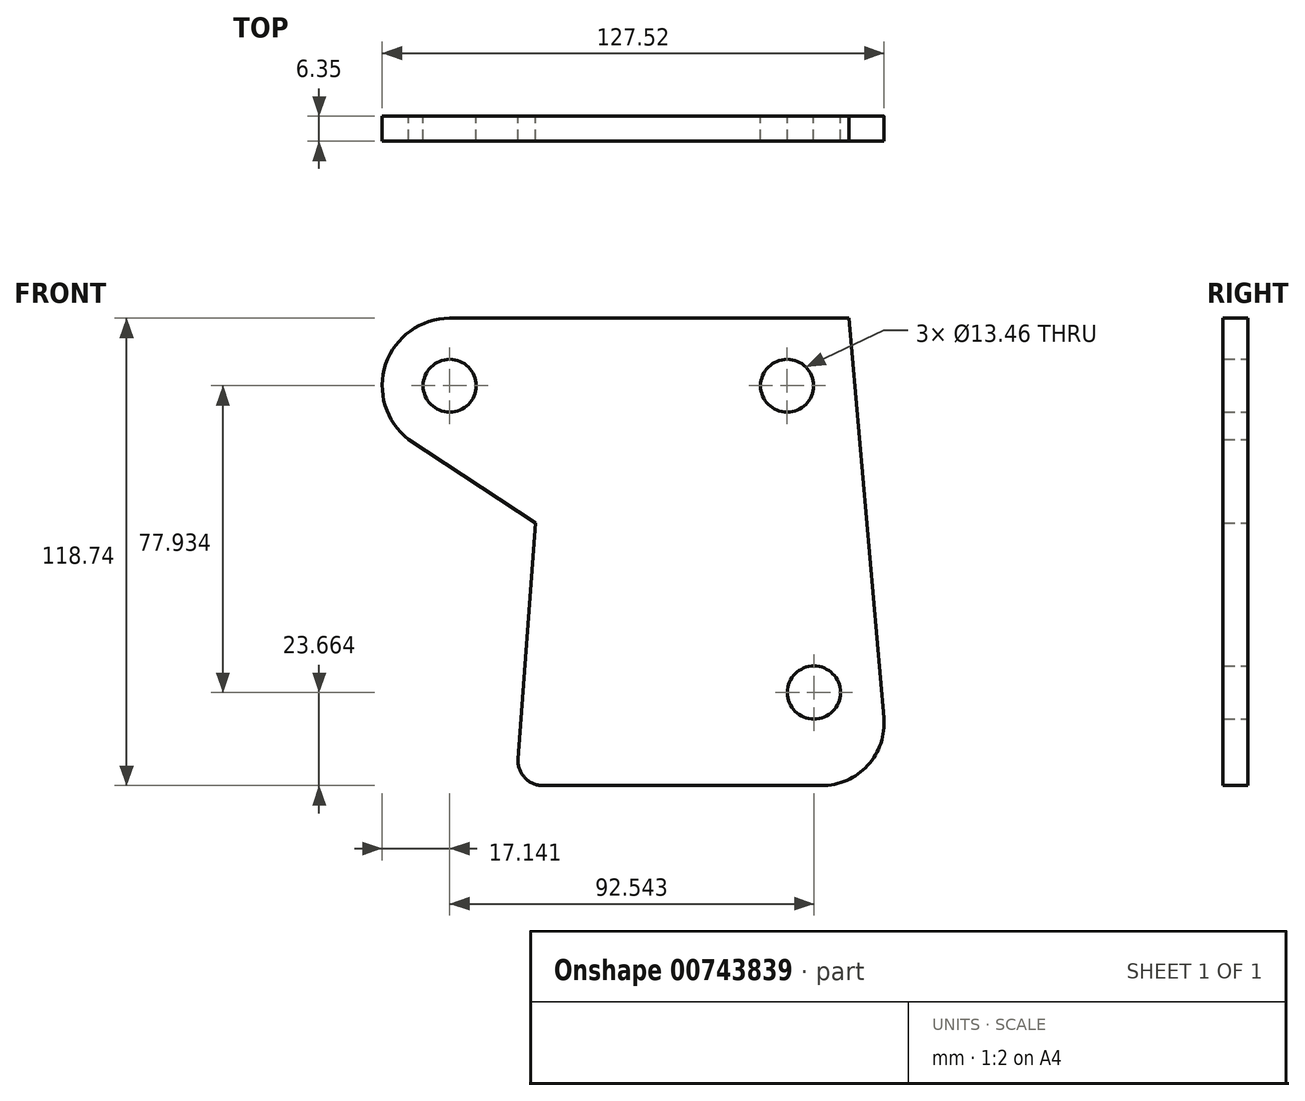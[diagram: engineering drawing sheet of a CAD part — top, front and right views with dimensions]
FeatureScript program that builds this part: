
annotation { "Feature Type Name" : "Feature", "Feature Type Description" : "" }
export const myFeature = defineFeature(function(context is Context, id is Id, definition is map)
    precondition{}
    {
        {
            var Q0;
            Q0=qCreatedBy(makeId("Front.planeOp"),FACE);
            var sketch = newSketch(context, id + "F0", { "sketchPlane" : qUnion([Q0])});
            skLineSegment(sketch, "E0", {"start": v(-32.41, -70.65) * mm, "end": v(-27.94, -10.8) * mm});
            skCircle(sketch, "E1", {"center": v(35.94, 24.13) * mm, "radius": 6.73 * mm});
            skCircle(sketch, "E2", {"center": v(-49.79, 24.13) * mm, "radius": 6.73 * mm});
            skCircle(sketch, "E3", {"center": v(42.75, -53.8) * mm, "radius": 6.73 * mm});
            skPoint(sketch, "E4.orphan", {"position": v(-68.32, 16.72) * mm});
            skPoint(sketch, "E5.orphan", {"position": v(-68.32, 36.83) * mm});
            skPoint(sketch, "E6.visualSharp", {"position": v(59.15, -77.47) * mm});
            skPoint(sketch, "E7.visualSharp", {"position": v(-32.92, -77.47) * mm});
            skArc(sketch, "E7.filletArc", {"start": v(-32.41, -70.65) * mm, "mid": v(-30.73, -75.44) * mm, "end": v(-26.08, -77.47) * mm});
            skPoint(sketch, "E8", {"position": v(-65.66, 24.13) * mm});
            skLineSegment(sketch, "E9", {"start": v(35.94, 40) * mm, "end": v(35.94, 40) * mm});
            skPoint(sketch, "E10.start.orphan", {"position": v(49.15, 36.83) * mm});
            skPoint(sketch, "E11.visualSharp", {"position": v(60.76, -77.47) * mm});
            skPoint(sketch, "E12.end.orphan", {"position": v(-60.2, 10.5) * mm});
            skLineSegment(sketch, "E13.0", {"start": v(50.48, 41.27) * mm, "end": v(51.65, 41.27) * mm});
            skLineSegment(sketch, "E13.1", {"start": v(48.88, 41.27) * mm, "end": v(50.48, 41.27) * mm});
            skLineSegment(sketch, "E13.2", {"start": v(35.94, 41.27) * mm, "end": v(48.88, 41.27) * mm});
            skLineSegment(sketch, "E13.3", {"start": v(35.94, 41.27) * mm, "end": v(-49.79, 41.27) * mm});
            skLineSegment(sketch, "E14", {"start": v(51.76, 40) * mm, "end": v(51.65, 41.27) * mm});
            skPoint(sketch, "E15.end.orphan", {"position": v(50.48, 40) * mm});
            skPoint(sketch, "E16.end.orphan", {"position": v(48.88, 40) * mm});
            skPoint(sketch, "E17.end.orphan", {"position": v(-49.79, 40) * mm});
            skLineSegment(sketch, "E18", {"start": v(-27.94, -10.8) * mm, "end": v(-60.2, 10.5) * mm});
            skArc(sketch, "E19", {"start": v(-49.79, 41.27) * mm, "mid": v(-66.03, 29.62) * mm, "end": v(-60.2, 10.5) * mm});
            skPoint(sketch, "E20.visualSharp", {"position": v(62.03, -77.47) * mm});
            skLineSegment(sketch, "E21", {"start": v(51.76, 40) * mm, "end": v(60.52, -60.21) * mm});
            skPoint(sketch, "E22.start.orphan", {"position": v(41.83, -77.47) * mm});
            skLineSegment(sketch, "E23", {"start": v(44.71, -77.47) * mm, "end": v(-26.08, -77.47) * mm});
            skArc(sketch, "E24.filletArc", {"start": v(44.71, -77.47) * mm, "mid": v(56.41, -72.32) * mm, "end": v(60.52, -60.21) * mm});
            skSolve(sketch);
        }
        {
            var Q0;
            Q0=makeQuery(id+"F0.imprint","IMPRINT",FACE,{"disambiguationData":[TD([[makeQuery(id+"F0.imprint","IMPRINT",EDGE,{"derivedFrom":sQuery(id+"F0.wireOp",EDGE,"E0")}),-1.0]])]});
            extrude(context, id + "F1", {"entities" : qUnion([Q0]), "depth" : 6.35 * mm, "offsetDistance" : 25.4 * mm});
        }
    });
